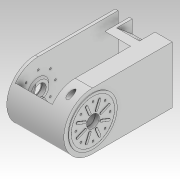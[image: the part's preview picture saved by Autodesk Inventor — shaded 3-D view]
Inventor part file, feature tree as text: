
AUTODESK INVENTOR PART (.ipt)
format: ipt  version: 2020 (Build 240168000, 168)  size: 651,776 bytes
history: native  units: mm
features: sketch x30, extrude x28, projected_geometry x6, plane x5, pattern_circular x2, fillet x2, revolve x2, chamfer x1, loft x1, other x1
ambient origin geometry x8: Origin, YZ Plane, XZ Plane, XY Plane, X Axis, Y Axis, Z Axis, Center Point
bodies: Solid1 (feature_tree)
feature tree (78):
  extrude  "Extrusion1"  Depth=50.0mm
  extrude  "Extrusion2"  Depth=100.0mm TaperAngle=0.0deg
  extrude  "Extrusion3"  TaperAngle=0.0deg  [1 undecoded]
  extrude  "Extrusion4"  Depth=10.0mm
  extrude  "Extrusion5"  Depth=30.0mm
  pattern_circular  "Circular Pattern1"  Count=8 Angle=360.0deg
  plane  "Work Plane1"
  plane  "Work Plane2"
  extrude  "Extrusion6"  Depth=30.0mm
  extrude  "Extrusion7"  Depth=10.0mm
  extrude  "Extrusion8"  Depth=10.0mm
  extrude  "Extrusion9"  [1 undecoded]
  chamfer  "Chamfer1"  Distance=10.0mm
  extrude  "Extrusion13"  Depth=10.0mm TaperAngle=0.0deg
  extrude  "Extrusion14"  Depth=3.0mm TaperAngle=0.0deg
  extrude  "Extrusion15"  Depth=3.0mm
  extrude  "Extrusion16"  Depth=3.0mm
  extrude  "Extrusion17"  Depth=80.0mm
  extrude  "Extrusion18"  Depth=60.0mm
  extrude  "Extrusion19"  Depth=80.0mm TaperAngle=360.0deg
  extrude  "Extrusion20"  Depth=15.5mm TaperAngle=0.0deg
  fillet  "Fillet2"  Radius=22.1mm
  pattern_circular  "Circular Pattern2"  Count=8 Angle=360.0deg
  extrude  "Extrusion21"  Depth=10.0mm
  extrude  "Extrusion22"  Depth=6.0mm
  plane  "Work Plane3"
  revolve  "Revolution1"  [1 undecoded]
  revolve  "Revolution2"  [1 undecoded]
  plane  "Work Plane4"
  extrude  "Extrusion23"  Depth=25.0mm
  extrude  "Extrusion24"  Depth=10.0mm
  fillet  "Fillet3"  Radius=96.8mm
  loft  "Loft1"
  extrude  "Extrusion25"  Depth=10.0mm
  extrude  "Extrusion26"  Depth=10.0mm
  extrude  "Extrusion27"  Depth=10.0mm
  extrude  "Extrusion28"  Depth=5.0mm
  plane  "Work Plane5"
  extrude  "Extrusion29"  Depth=10.0mm
  extrude  "Extrusion30"  TaperAngle=90.0deg  [1 undecoded]
  extrude  "Extrusion32"  Depth=10.0mm
  sketch  "Sketch1"  dims[d0=50.0mm d1=250.0mm]
  sketch  "Sketch2"  dims[d2=50.0mm d3=100.0mm d4=0.0mm]
  sketch  "Sketch4"  dims[d5=5.0mm d7=0.0mm d8=0.0mm]
  sketch  "Sketch5"  dims[d11=10.0mm d12=0.0mm d14=85.0mm]
  sketch  "Sketch7"  dims[d15=1.0mm d16=0.0mm d17=30.0mm]
  projected_geometry  "Projected Loop1"
  sketch  "Sketch8"  dims[d18=3.3mm]
  projected_geometry  "Projected Loop2"
  projected_geometry  "Projected Loop4"
  sketch  "Sketch9"  dims[d19=15.0mm d20=0.0mm d21=80.0mm d22=360.0deg]
  sketch  "Sketch10"  dims[d24=30.0mm d25=30.0mm]
  sketch  "Sketch14"  dims[d30=-5.0mm d31=10.0mm]
  sketch  "Sketch15"  dims[d32=10.0mm d33=10.0mm]
  sketch  "Sketch16"  dims[d34=31.5mm d35=0.0mm d36=-5.0mm d38=10.0mm d39=0.0mm]
  sketch  "Sketch17"  dims[d40=22.1mm d41=10.0mm d42=0.0mm]
  sketch  "Sketch18"  dims[d43=5.0mm d44=3.0mm d45=0.0mm]
  sketch  "Sketch19"  dims[d56=3.0mm d57=2.0mm d58=45.0deg d62=95.1mm]
  sketch  "Sketch20"  dims[d63=10.0mm d64=0.0mm d65=3.0mm]
  sketch  "Sketch21"  dims[d66=0.5mm d67=0.0mm d68=80.0mm]
  sketch  "Sketch22"  dims[d69=15.5mm d70=0.0mm d71=60.0mm]
  sketch  "Sketch23"  dims[d72=3.2mm d73=80.0mm d75=360.0deg]
  other  "Work Axis1"
  sketch  "Sketch24"  dims[d77=15.5mm d78=0.0mm d79=15.5mm d80=0.0mm d81=22.1mm]
  projected_geometry  "Projected Loop5"
  projected_geometry  "Projected Loop6"
  sketch  "Sketch26"  dims[d82=0.0mm d83=0.0mm]
  sketch  "Sketch27"  dims[d84=76.0mm]
  sketch  "Sketch28"  dims[d85=0.1mm d86=0.0mm]
  sketch  "Sketch29"  dims[d87=15.0mm]
  sketch  "Sketch30"  dims[d88=2.0mm]
  sketch  "Sketch31"  dims[d89=22.5mm]
  sketch  "Sketch32"  dims[d90=0.8mm d91=0.0mm]
  sketch  "Sketch33"  dims[d92=0.2mm d93=80.0mm d94=360.0deg]
  projected_geometry  "Projected Loop7"
  sketch  "Sketch34"  dims[d96=24.43461mm d97=10.0mm]
  sketch  "Sketch35"  dims[d98=8.0mm d99=6.0mm]
  sketch  "Sketch38"  dims[d100=8.0mm d101=6.0mm d102=23.749mm d103=0.0mm d104=25.0mm d105=16.1mm d106=96.8mm d107=0.0mm d108=0.0mm d109=2.5mm d110=5.2mm d111=1.0mm d112=5.0mm d113=5.2mm d114=90.0deg d115=15.0mm d116=25.0mm d117=25.0mm d118=19.0mm d119=19.0mm d120=2.7mm d122=4.0mm d123=0.0mm d124=5.5mm d125=2.0mm d126=0.0mm d127=90.0deg d128=2.0mm d129=18.8mm d130=0.0mm d131=111.25mm d132=0.0mm d133=6.0mm d134=4.0mm d135=0.0mm d136=1.0mm d137=1.0mm d138=0.0mm d139=-7.0mm d140=1.0mm d141=1.0mm d142=0.0mm d143=7.0mm d144=5.0mm d145=6.0mm d146=0.0mm d147=90.0deg d148=0.0mm d149=90.0deg d150=3.0mm d151=10.0mm d152=0.0mm d155=110.0mm d156=0.0mm d157=0.0mm d159=30.0deg d160=6.0mm]
note: 5 required parameter values undecoded (feature->parameter linkage not recoverable at this tier; creation-order binding heuristic only, values carry confidence <= 0.55)